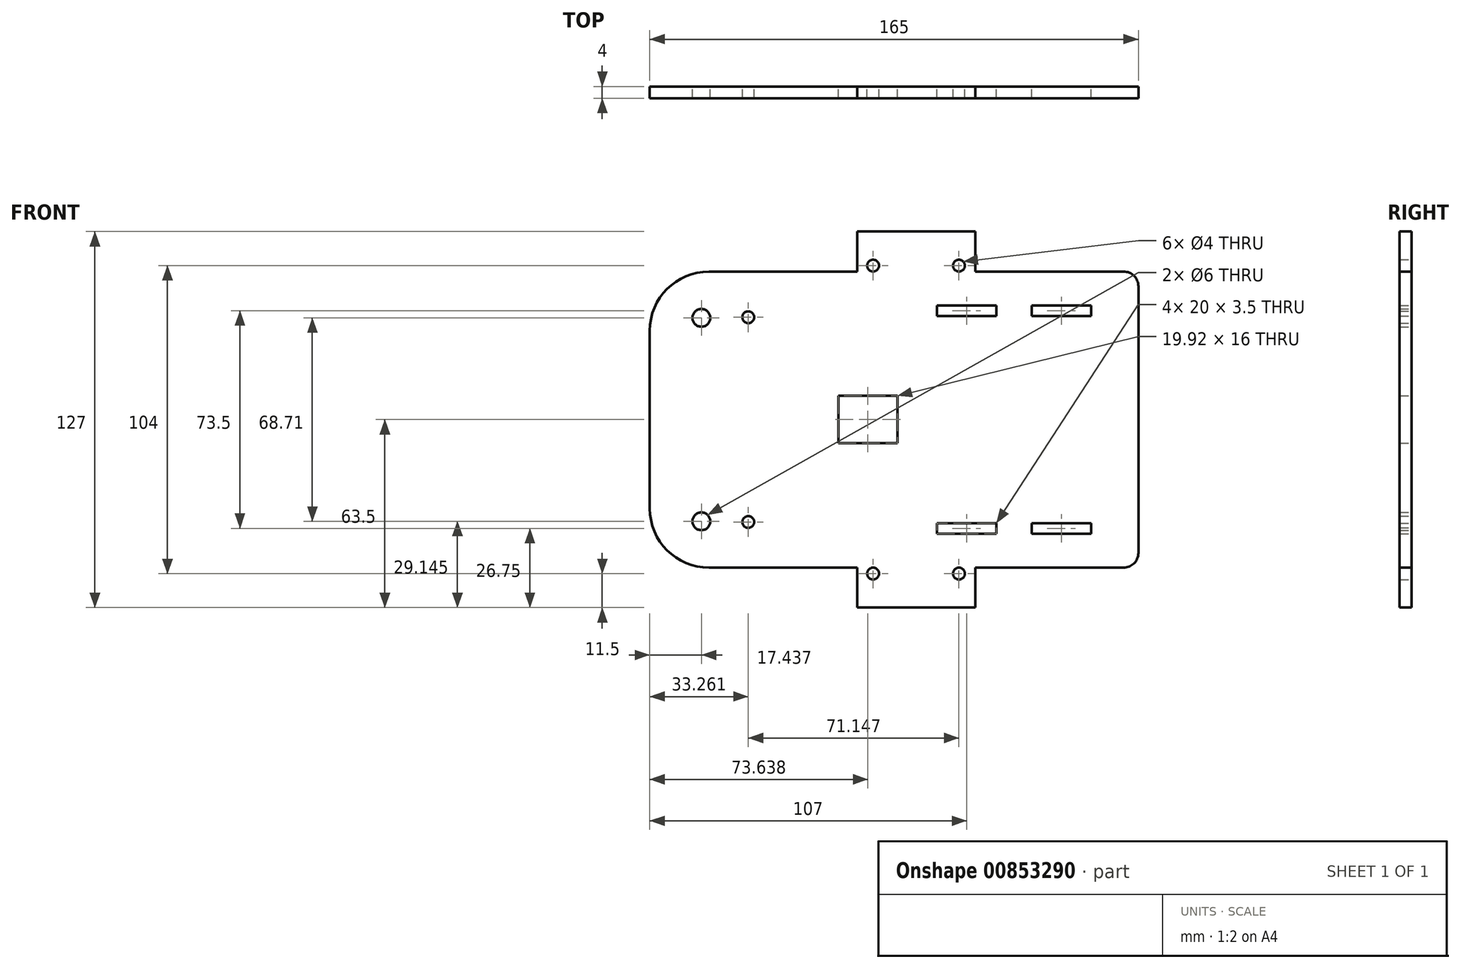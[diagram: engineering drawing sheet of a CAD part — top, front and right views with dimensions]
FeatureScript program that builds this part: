
annotation { "Feature Type Name" : "Feature", "Feature Type Description" : "" }
export const myFeature = defineFeature(function(context is Context, id is Id, definition is map)
    precondition{}
    {
        {
            var Q0;
            Q0=qCreatedBy(makeId("Front.planeOp"),FACE);
            var sketch = newSketch(context, id + "F0", { "sketchPlane" : qUnion([Q0])});
            skLineSegment(sketch, "E0.0", {"start": v(64, 35) * mm, "end": v(64, 38.5) * mm});
            skLineSegment(sketch, "E1.0", {"start": v(44, 35) * mm, "end": v(44, 38.5) * mm});
            skLineSegment(sketch, "E2.trimOffspring", {"start": v(44, 38.5) * mm, "end": v(64, 38.5) * mm});
            skLineSegment(sketch, "E3.trimOffspring", {"start": v(44, 35) * mm, "end": v(64, 35) * mm});
            skLineSegment(sketch, "E4.MirrorCS", {"start": v(32, 38.5) * mm, "end": v(12, 38.5) * mm});
            skLineSegment(sketch, "E5.MirrorCS", {"start": v(32, 35) * mm, "end": v(12, 35) * mm});
            skLineSegment(sketch, "E6.MirrorCS", {"start": v(32, 35) * mm, "end": v(32, 38.5) * mm});
            skLineSegment(sketch, "E7.MirrorCS", {"start": v(12, 35) * mm, "end": v(12, 38.5) * mm});
            skLineSegment(sketch, "E8.MirrorCS", {"start": v(44, -38.5) * mm, "end": v(64, -38.5) * mm});
            skLineSegment(sketch, "E9.MirrorCS", {"start": v(32, -35) * mm, "end": v(32, -38.5) * mm});
            skLineSegment(sketch, "E10.MirrorCS", {"start": v(64, -35) * mm, "end": v(64, -38.5) * mm});
            skLineSegment(sketch, "E11.MirrorCS", {"start": v(12, -35) * mm, "end": v(12, -38.5) * mm});
            skLineSegment(sketch, "E12.MirrorCS", {"start": v(44, -35) * mm, "end": v(64, -35) * mm});
            skLineSegment(sketch, "E13.MirrorCS", {"start": v(44, -35) * mm, "end": v(44, -38.5) * mm});
            skLineSegment(sketch, "E14.MirrorCS", {"start": v(32, -35) * mm, "end": v(12, -35) * mm});
            skLineSegment(sketch, "E15.MirrorCS", {"start": v(32, -38.5) * mm, "end": v(12, -38.5) * mm});
            skLineSegment(sketch, "E16", {"start": v(80, 45) * mm, "end": v(80, -45) * mm});
            skLineSegment(sketch, "E17.0", {"start": v(-1.4, 8) * mm, "end": v(-1.4, -8) * mm});
            skPoint(sketch, "E18.orphan", {"position": v(-35.9, 0) * mm});
            skPoint(sketch, "E19.orphan", {"position": v(-71, 57.24) * mm});
            skPoint(sketch, "E20.orphan", {"position": v(-80, 50) * mm});
            skPoint(sketch, "E21.orphan", {"position": v(-71, -57.24) * mm});
            skPoint(sketch, "E22.orphan", {"position": v(-80, -50) * mm});
            skLineSegment(sketch, "E23", {"start": v(-85, 30) * mm, "end": v(-85, -30) * mm});
            skLineSegment(sketch, "E24", {"start": v(-65, 50) * mm, "end": v(-15, 50) * mm});
            skLineSegment(sketch, "E25", {"start": v(-65, -50) * mm, "end": v(-15, -50) * mm});
            skPoint(sketch, "E26.visualSharp", {"position": v(80, 50) * mm});
            skArc(sketch, "E26.filletArc", {"start": v(80, 45) * mm, "mid": v(78.54, 48.54) * mm, "end": v(75, 50) * mm});
            skPoint(sketch, "E27.visualSharp", {"position": v(80, -50) * mm});
            skArc(sketch, "E27.filletArc", {"start": v(75, -50) * mm, "mid": v(78.54, -48.54) * mm, "end": v(80, -45) * mm});
            skCircle(sketch, "E28", {"center": v(-67.56, 34.36) * mm, "radius": 3 * mm});
            skCircle(sketch, "E29.MirrorC", {"center": v(-67.56, -34.36) * mm, "radius": 3 * mm});
            skPoint(sketch, "E30.visualSharp", {"position": v(-85, 50) * mm});
            skArc(sketch, "E30.filletArc", {"start": v(-65, 50) * mm, "mid": v(-79.14, 44.14) * mm, "end": v(-85, 30) * mm});
            skPoint(sketch, "E31.visualSharp", {"position": v(-85, -50) * mm});
            skArc(sketch, "E31.filletArc", {"start": v(-85, -30) * mm, "mid": v(-79.14, -44.14) * mm, "end": v(-65, -50) * mm});
            skLineSegment(sketch, "E32.0", {"start": v(-15, -50) * mm, "end": v(-15, -63.5) * mm});
            skCircle(sketch, "E33", {"center": v(-9.6, -52) * mm, "radius": 2 * mm});
            skCircle(sketch, "E34.MirrorC", {"center": v(19.4, -52) * mm, "radius": 2 * mm});
            skLineSegment(sketch, "E35.MirrorCS", {"start": v(24.9, -50) * mm, "end": v(24.9, -63.5) * mm});
            skLineSegment(sketch, "E36.MirrorCS", {"start": v(24.9, -63.5) * mm, "end": v(-15, -63.5) * mm});
            skLineSegment(sketch, "E37.trimOffspring", {"start": v(24.9, -50) * mm, "end": v(75, -50) * mm});
            skCircle(sketch, "E38.MirrorC", {"center": v(19.4, 52) * mm, "radius": 2 * mm});
            skCircle(sketch, "E39.MirrorC", {"center": v(-9.6, 52) * mm, "radius": 2 * mm});
            skLineSegment(sketch, "E40.MirrorCS", {"start": v(-15, 50) * mm, "end": v(-15, 63.5) * mm});
            skLineSegment(sketch, "E41.MirrorCS", {"start": v(24.9, 63.5) * mm, "end": v(-15, 63.5) * mm});
            skLineSegment(sketch, "E42.MirrorCS", {"start": v(24.9, 50) * mm, "end": v(24.9, 63.5) * mm});
            skLineSegment(sketch, "E43.trimOffspring", {"start": v(24.9, 50) * mm, "end": v(75, 50) * mm});
            skCircle(sketch, "E44", {"center": v(-51.74, 34.57) * mm, "radius": 2 * mm});
            skCircle(sketch, "E45.MirrorC", {"center": v(-51.74, -34.57) * mm, "radius": 2 * mm});
            skLineSegment(sketch, "E46", {"start": v(-1.4, -8) * mm, "end": v(-21.32, -8) * mm});
            skPoint(sketch, "E47.orphan", {"position": v(-1.4, -12.6) * mm});
            skLineSegment(sketch, "E48.MirrorCS", {"start": v(-1.4, 8) * mm, "end": v(-21.32, 8) * mm});
            skPoint(sketch, "E49.orphan", {"position": v(-1.4, 12.6) * mm});
            skLineSegment(sketch, "E50", {"start": v(-21.32, 8) * mm, "end": v(-21.32, -8) * mm});
            skSolve(sketch);
        }
        {
            var Q0;
            Q0 = qSketchRegion(id + "F0", true);
            extrude(context, id + "F1", {"entities" : qUnion([Q0]), "depth" : 4 * mm, "offsetDistance" : 25 * mm});
        }
    });
